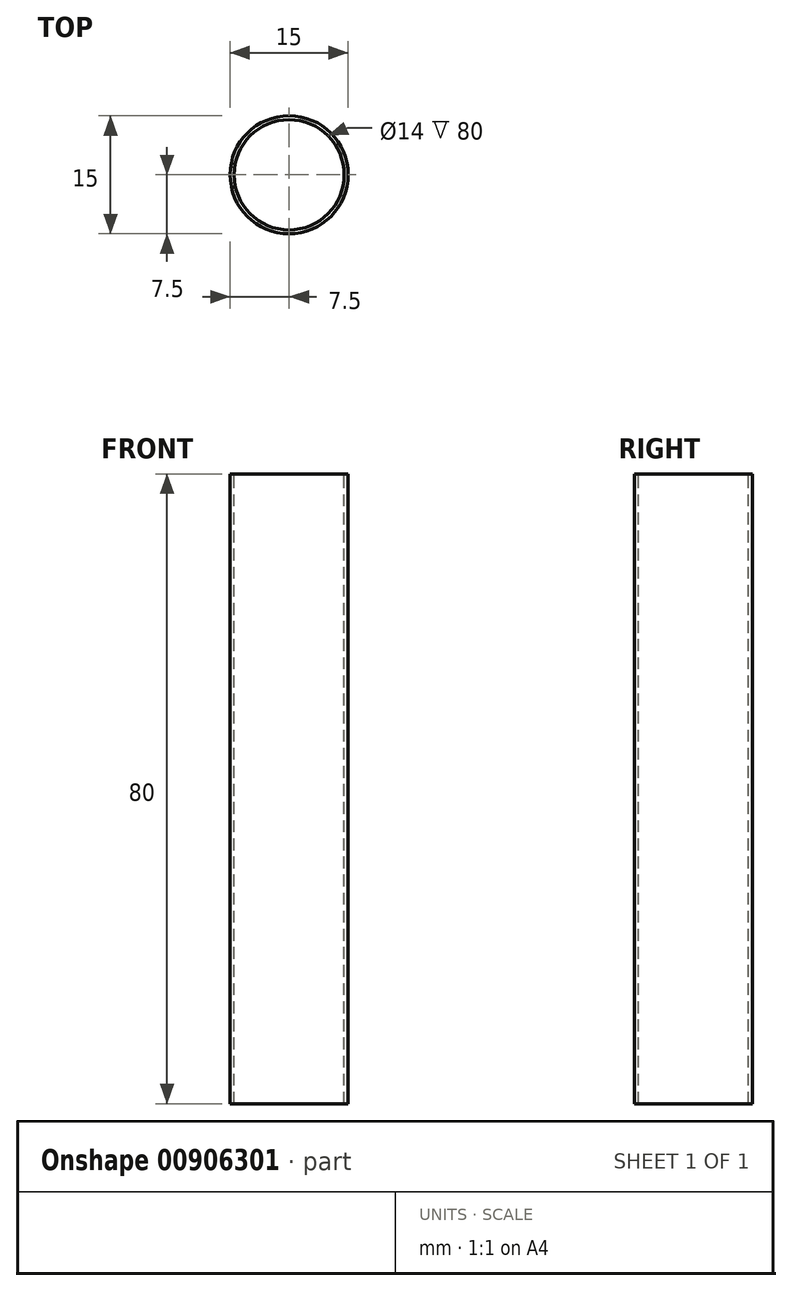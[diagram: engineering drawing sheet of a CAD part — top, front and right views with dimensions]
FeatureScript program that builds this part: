
annotation { "Feature Type Name" : "Feature", "Feature Type Description" : "" }
export const myFeature = defineFeature(function(context is Context, id is Id, definition is map)
    precondition{}
    {
        {
            var Q0;
            Q0=qCreatedBy(makeId("Top.planeOp"),FACE);
            var sketch = newSketch(context, id + "F0", { "sketchPlane" : qUnion([Q0])});
            skCircle(sketch, "E0", {"center": v(0, 0) * mm, "radius": 7.5 * mm});
            skCircle(sketch, "E1", {"center": v(0, 0) * mm, "radius": 7 * mm});
            skSolve(sketch);
        }
        {
            var Q0;
            Q0=qCreatedBy(makeId("Front.planeOp"),FACE);
            var sketch = newSketch(context, id + "F1", { "sketchPlane" : qUnion([Q0])});
            skLineSegment(sketch, "E2", {"start": v(0, 0) * mm, "end": v(0, 80) * mm});
            skSolve(sketch);
        }
        {
            var Q0;
            Q0=makeQuery(id+"F0.imprint","IMPRINT",FACE,{"disambiguationData":[TD([[makeQuery(id+"F0.imprint","IMPRINT",EDGE,{"derivedFrom":sQuery(id+"F0.wireOp",EDGE,"E0")}),1.0]])]});
            var Q1;
            Q1=sQuery(id+"F1.wireOp",EDGE,"E2");
            sweep(context, id + "F2", {"profiles" : qUnion([Q0]), "path" : qUnion([Q1])});
        }
    });
